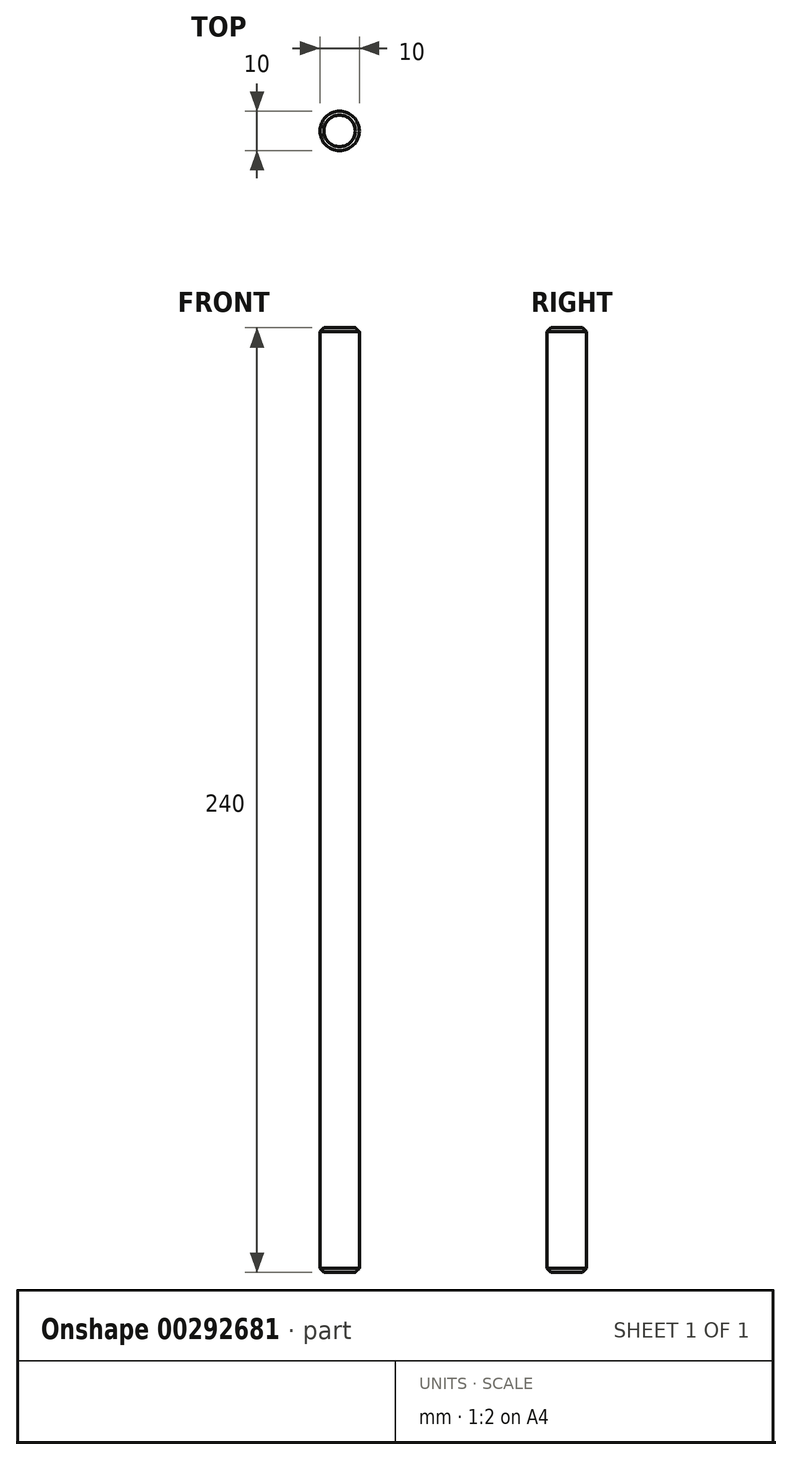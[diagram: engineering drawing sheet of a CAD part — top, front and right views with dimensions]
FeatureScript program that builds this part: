
annotation { "Feature Type Name" : "Feature", "Feature Type Description" : "" }
export const myFeature = defineFeature(function(context is Context, id is Id, definition is map)
    precondition{}
    {
        {
            var Q0;
            Q0=qCreatedBy(makeId("Top.planeOp"),FACE);
            var sketch = newSketch(context, id + "F0", { "sketchPlane" : qUnion([Q0])});
            skCircle(sketch, "E0", {"center": v(0, 0) * mm, "radius": 5 * mm});
            skSolve(sketch);
        }
        {
            var Q0;
            Q0=makeQuery(id+"F0.imprint","IMPRINT",FACE,{"disambiguationData":[TD([[makeQuery(id+"F0.imprint","IMPRINT",EDGE,{"derivedFrom":sQuery(id+"F0.wireOp",EDGE,"E0")}),1.0]])]});
            extrude(context, id + "F1", {"entities" : qUnion([Q0]), "depth" : 240 * mm, "offsetDistance" : 25 * mm});
        }
        {
            var Q0;
            Q0=makeQuery(id+"F1.opExtrude","CAP_EDGE",EDGE,{"disambiguationData":[OSD([sQuery(id+"F0.wireOp",EDGE,"E0")])],"isStart":true});
            var Q1;
            Q1=makeQuery(id+"F1.opExtrude","CAP_EDGE",EDGE,{"disambiguationData":[OSD([sQuery(id+"F0.wireOp",EDGE,"E0")])],"isStart":false});
            chamfer(context, id + "F2", {"entities" : qUnion([Q0, Q1]), "width" : 1 * mm, "tangentPropagation" : true});
        }
    });
